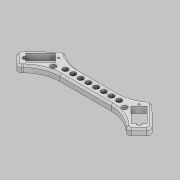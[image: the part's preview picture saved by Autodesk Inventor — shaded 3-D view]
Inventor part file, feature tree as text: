
AUTODESK INVENTOR PART (.ipt)
format: ipt  version: 2022.2 (Build 262287010, 287A)  size: 280,064 bytes
history: native  units: mm
features: extrude x6, sketch x6, fillet x2, other x1, chamfer x1
ambient origin geometry x8: Origin, YZ Plane, XZ Plane, XY Plane, X Axis, Y Axis, Z Axis, Center Point
bodies: Body1 (feature_tree)
feature tree (16):
  other  "Sólido1"
  extrude  "Extrusión1"  Depth=15.0mm
  fillet  "Empalme1"  Radius=20.0mm
  extrude  "Extrusión2"  TaperAngle=0.0deg  [1 undecoded]
  extrude  "Extrusión3"  Depth=3.0mm
  extrude  "Extrusión4"  Depth=7.0mm TaperAngle=0.0deg
  extrude  "Extrusión5"  Depth=5.5mm
  extrude  "Extrusión6"  Depth=2.0mm
  fillet  "Empalme3"  Radius=40.0mm
  chamfer  "Chaflán2"  Distance=7.0mm
  sketch  "Boceto1"  dims[d1=10.0mm d2=15.0mm d4=20.0mm]
  sketch  "Boceto2"  dims[d5=37.0mm d6=0.0mm]
  sketch  "Boceto4"  dims[d7=3.0mm d10=3.8mm]
  sketch  "Boceto5"  dims[d11=39.0mm d14=7.0mm d15=0.0mm]
  sketch  "Boceto6"  dims[d16=40.0mm d17=5.5mm]
  sketch  "Boceto7"  dims[d18=7.5mm d19=4.2mm d20=40.0mm d22=8.4mm d23=10.0mm d25=10.0mm d27=7.0mm d28=0.0mm d32=12.5mm d33=23.0mm d34=10.0mm d35=0.0mm d36=6.0mm d37=6.0mm d38=2.0mm d39=0.0mm d44=4.5mm d45=2.0mm d46=10.0mm d47=0.0mm d48=2.0mm d49=2.0mm d50=27.7mm d51=6.25mm d52=10.0mm d53=0.0mm d62=4.0mm d63=2.0mm d64=2.0mm d65=45.0deg]
note: 1 required parameter value undecoded (feature->parameter linkage not recoverable at this tier; creation-order binding heuristic only, values carry confidence <= 0.55)
